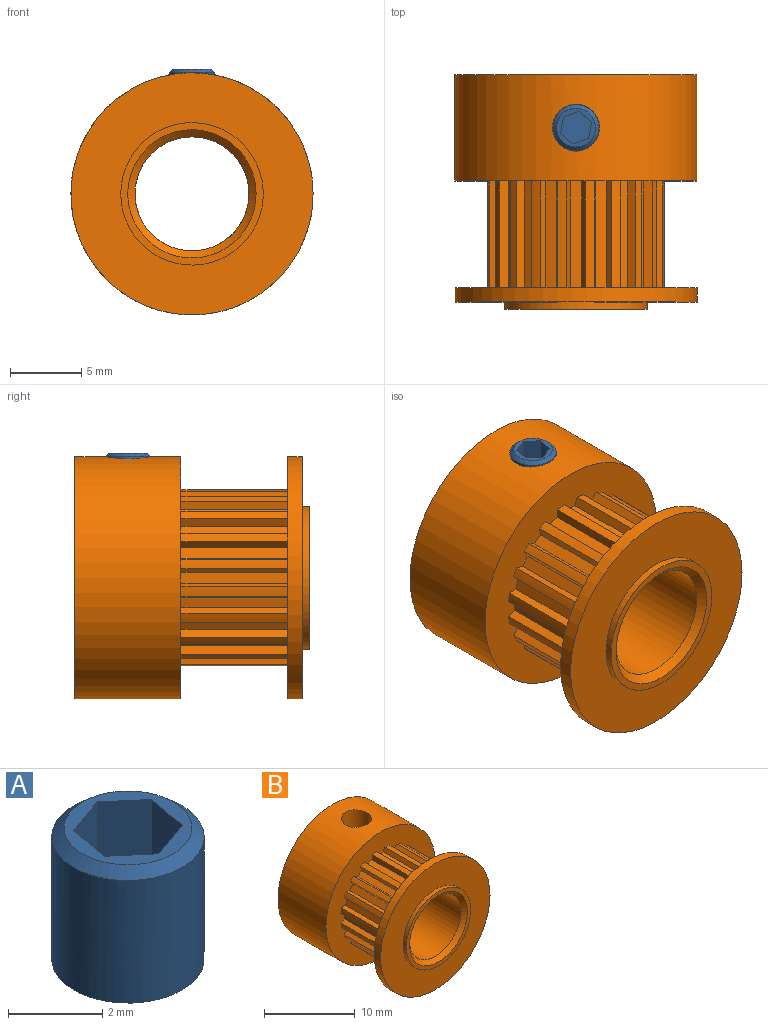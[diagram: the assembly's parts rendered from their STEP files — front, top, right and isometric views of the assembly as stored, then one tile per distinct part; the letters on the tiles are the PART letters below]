
ASSEMBLY  parts=2 mates=1
PART A: 12 faces, bbox 3.2x3.2x4 mm
  f0: plane 3x1.09mm, normal (-0.33,0.94,0), area 3.5mm2, adj f1,f2,f4,f7
  f1: plane 3x0.88mm, normal (0.65,0.76,0), area 3.5mm2, adj f0,f3,f4,f7
  f2: plane 3x1.14mm, normal (-0.98,0.18,0), area 3.5mm2, adj f0,f4,f5,f7
  f3: plane 3x1.14mm, normal (0.98,-0.18,0), area 3.5mm2, adj f1,f4,f6,f7
  f4: plane 2.27x2.18mm, normal (0,0,1), area 3.5mm2, adj f0,f1,f2,f3,f5,f6
  f5: plane 3x0.88mm, normal (-0.65,-0.76,0), area 3.5mm2, adj f2,f4,f6,f7
  f6: plane 3x1.09mm, normal (0.33,-0.94,0), area 3.5mm2, adj f3,f4,f5,f7
  f7: plane 2.71x2.71mm, normal (0,0,1), area 2.3mm2, adj f0,f1,f2,f3,f5,f6,f9
  f8: plane 1.19x1.19mm, normal (0,0,-1), area 1.1mm2, adj f10
  f9: cone r=1.61mm half-angle=48.9deg, axis (0,0,-1), area 3.2mm2, adj f7,f11
  f10: cone r=1.61mm half-angle=59.8deg, axis (0,0,1), area 8.2mm2, adj f8,f11
  f11: cylinder r=1.61mm len=3.23mm, axis (0,0,-1), area 32.3mm2, adj f9,f10
PART B: 92 faces, bbox 17x16.5x17 mm
  f0: plane 7.5x0.63mm, normal (1,0,-0.08), area 4.7mm2, adj f1,f2,f81,f88
  f1: plane 7.5x0.76mm, normal (0.31,0,-0.95), area 6mm2, adj f0,f3,f81,f88
  f2: cylinder r=6.21mm len=7.5mm, axis (0,1,0), area 5mm2, adj f0,f4,f81,f88
  f3: plane 7.5x0.48mm, normal (-0.76,0,-0.65), area 4.7mm2, adj f1,f5,f81,f88
  f4: plane 7.5x0.58mm, normal (-0.92,0,-0.38), area 4.7mm2, adj f2,f6,f81,f88
  f5: cylinder r=6.21mm len=7.5mm, axis (0,1,0), area 5mm2, adj f3,f7,f81,f88
  f6: plane 7.5x0.8mm, normal (0,0,-1), area 6mm2, adj f4,f8,f81,f88
  f7: plane 7.5x0.61mm, normal (0.97,0,0.23), area 4.7mm2, adj f5,f9,f81,f88
  f8: plane 7.5x0.58mm, normal (0.92,0,-0.38), area 4.7mm2, adj f6,f10,f81,f88
  f9: plane 7.5x0.65mm, normal (0.59,0,-0.81), area 6mm2, adj f7,f11,f81,f88
  f10: cylinder r=6.21mm len=7.5mm, axis (0,1,0), area 5mm2, adj f8,f12,f81,f88
  f11: plane 7.5x0.54mm, normal (-0.52,0,-0.85), area 4.7mm2, adj f9,f13,f81,f88
  f12: plane 7.5x0.63mm, normal (-1,0,-0.08), area 4.7mm2, adj f10,f14,f81,f88
  f13: cylinder r=6.21mm len=7.5mm, axis (0,1,0), area 5mm2, adj f11,f15,f81,f88
  f14: plane 7.5x0.76mm, normal (-0.31,0,-0.95), area 6mm2, adj f12,f16,f81,f88
  f15: plane 7.5x0.54mm, normal (0.85,0,0.52), area 4.7mm2, adj f13,f17,f81,f88
  f16: plane 7.5x0.48mm, normal (0.76,0,-0.65), area 4.7mm2, adj f14,f18,f81,f88
  f17: plane 7.5x0.65mm, normal (0.81,0,-0.59), area 6mm2, adj f15,f19,f81,f88
  f18: cylinder r=6.21mm len=7.5mm, axis (0,1,0), area 5mm2, adj f16,f20,f81,f88
  f19: plane 7.5x0.61mm, normal (-0.23,0,-0.97), area 4.7mm2, adj f17,f21,f81,f88
  f20: plane 7.5x0.61mm, normal (-0.97,0,0.23), area 4.7mm2, adj f18,f22,f81,f88
  f21: cylinder r=6.21mm len=7.5mm, axis (0,1,0), area 5mm2, adj f19,f23,f81,f88
  f22: plane 7.5x0.65mm, normal (-0.59,0,-0.81), area 6mm2, adj f20,f24,f81,f88
  f23: plane 7.5x0.48mm, normal (0.65,0,0.76), area 4.7mm2, adj f21,f25,f81,f88
  f24: plane 7.5x0.54mm, normal (0.52,0,-0.85), area 4.7mm2, adj f22,f26,f81,f88
  f25: plane 7.5x0.76mm, normal (0.95,0,-0.31), area 6mm2, adj f23,f27,f81,f88
  f26: cylinder r=6.21mm len=7.5mm, axis (0,1,0), area 5mm2, adj f24,f28,f81,f88
  f27: plane 7.5x0.63mm, normal (0.08,0,-1), area 4.7mm2, adj f25,f29,f81,f88
  f28: plane 7.5x0.54mm, normal (-0.85,0,0.52), area 4.7mm2, adj f26,f30,f81,f88
  f29: cylinder r=6.21mm len=7.5mm, axis (0,1,0), area 5mm2, adj f27,f31,f81,f88
  f30: plane 7.5x0.65mm, normal (-0.81,0,-0.59), area 6mm2, adj f28,f32,f81,f88
  f31: plane 7.5x0.58mm, normal (0.38,0,0.92), area 4.7mm2, adj f29,f33,f81,f88
  f32: plane 7.5x0.61mm, normal (0.23,0,-0.97), area 4.7mm2, adj f30,f34,f81,f88
  f33: plane 7.5x0.8mm, normal (1,0,0), area 6mm2, adj f31,f35,f81,f88
  f34: cylinder r=6.21mm len=7.5mm, axis (0,1,0), area 5mm2, adj f32,f36,f81,f88
  f35: plane 7.5x0.58mm, normal (0.38,0,-0.92), area 4.7mm2, adj f33,f37,f81,f88
  f36: plane 7.5x0.48mm, normal (-0.65,0,0.76), area 4.7mm2, adj f34,f38,f81,f88
  f37: cylinder r=6.21mm len=7.5mm, axis (0,1,0), area 5mm2, adj f35,f39,f81,f88
  f38: plane 7.5x0.76mm, normal (-0.95,0,-0.31), area 6mm2, adj f36,f40,f81,f88
  f39: plane 7.5x0.63mm, normal (0.08,0,1), area 4.7mm2, adj f37,f41,f81,f88
  f40: plane 7.5x0.63mm, normal (-0.08,0,-1), area 4.7mm2, adj f38,f42,f81,f88
  f41: plane 7.5x0.76mm, normal (0.95,0,0.31), area 6mm2, adj f39,f43,f81,f88
  f42: cylinder r=6.21mm len=7.5mm, axis (0,1,0), area 5mm2, adj f40,f44,f81,f88
  f43: plane 7.5x0.48mm, normal (0.65,0,-0.76), area 4.7mm2, adj f41,f45,f81,f88
  f44: plane 7.5x0.58mm, normal (-0.38,0,0.92), area 4.7mm2, adj f42,f46,f81,f88
  f45: cylinder r=6.21mm len=7.5mm, axis (0,1,0), area 5mm2, adj f43,f47,f81,f88
  f46: plane 7.5x0.8mm, normal (-1,0,0), area 6mm2, adj f44,f48,f81,f88
  f47: plane 7.5x0.61mm, normal (-0.23,0,0.97), area 4.7mm2, adj f45,f49,f81,f88
  f48: plane 7.5x0.58mm, normal (-0.38,0,-0.92), area 4.7mm2, adj f46,f50,f81,f88
  f49: plane 7.5x0.65mm, normal (0.81,0,0.59), area 6mm2, adj f47,f51,f81,f88
  f50: cylinder r=6.21mm len=7.5mm, axis (0,1,0), area 5mm2, adj f48,f52,f81,f88
  f51: plane 7.5x0.54mm, normal (0.85,0,-0.52), area 4.7mm2, adj f49,f53,f81,f88
  f52: plane 7.5x0.63mm, normal (-0.08,0,1), area 4.7mm2, adj f50,f54,f81,f88
  f53: cylinder r=6.21mm len=7.5mm, axis (0,1,0), area 5mm2, adj f51,f55,f81,f88
  f54: plane 7.5x0.76mm, normal (-0.95,0,0.31), area 6mm2, adj f52,f56,f81,f88
  f55: plane 7.5x0.54mm, normal (-0.52,0,0.85), area 4.7mm2, adj f53,f57,f81,f88
  f56: plane 7.5x0.48mm, normal (-0.65,0,-0.76), area 4.7mm2, adj f54,f58,f81,f88
  f57: plane 7.5x0.65mm, normal (0.59,0,0.81), area 6mm2, adj f55,f59,f81,f88
  f58: cylinder r=6.21mm len=7.5mm, axis (0,1,0), area 5mm2, adj f56,f60,f81,f88
  f59: plane 7.5x0.61mm, normal (0.97,0,-0.23), area 4.7mm2, adj f57,f61,f81,f88
  f60: plane 7.5x0.61mm, normal (0.23,0,0.97), area 4.7mm2, adj f58,f62,f81,f88
  f61: cylinder r=6.21mm len=7.5mm, axis (0,1,0), area 5mm2, adj f59,f63,f81,f88
  f62: plane 7.5x0.65mm, normal (-0.81,0,0.59), area 6mm2, adj f60,f64,f81,f88
  f63: plane 7.5x0.48mm, normal (-0.76,0,0.65), area 4.7mm2, adj f61,f65,f81,f88
  f64: plane 7.5x0.54mm, normal (-0.85,0,-0.52), area 4.7mm2, adj f62,f66,f81,f88
  f65: plane 7.5x0.76mm, normal (0.31,0,0.95), area 6mm2, adj f63,f67,f81,f88
  f66: cylinder r=6.21mm len=7.5mm, axis (0,1,0), area 5mm2, adj f64,f68,f81,f88
  f67: plane 7.5x0.63mm, normal (1,0,0.08), area 4.7mm2, adj f65,f69,f81,f88
  f68: plane 7.5x0.54mm, normal (0.52,0,0.85), area 4.7mm2, adj f66,f70,f81,f88
  f69: cylinder r=6.21mm len=7.5mm, axis (0,1,0), area 5mm2, adj f67,f71,f81,f88
  f70: plane 7.5x0.65mm, normal (-0.59,0,0.81), area 6mm2, adj f68,f72,f81,f88
  f71: plane 7.5x0.58mm, normal (-0.92,0,0.38), area 4.7mm2, adj f69,f74,f81,f88
  f72: plane 7.5x0.61mm, normal (-0.97,0,-0.23), area 4.7mm2, adj f70,f75,f81,f88
  f73: plane 17x17mm, normal (0,-1,0), area 148.4mm2, adj f76,f77
  f74: plane 7.5x0.8mm, normal (0,0,1), area 6mm2, adj f71,f78,f81,f88
  f75: cylinder r=6.21mm len=7.5mm, axis (0,1,0), area 5mm2, adj f72,f79,f81,f88
  f76: cylinder r=5mm len=10mm, axis (0,1,0), area 15.7mm2, adj f73,f80
  f77: cylinder r=8.5mm len=17mm, axis (0,-1,0), area 53.4mm2, adj f73,f81
  f78: plane 7.5x0.58mm, normal (0.92,0,0.38), area 4.7mm2, adj f74,f81,f82,f88
  f79: plane 7.5x0.48mm, normal (0.76,0,0.65), area 4.7mm2, adj f75,f81,f83,f88
  f80: plane 10x10mm, normal (0,-1,0), area 14.9mm2, adj f76,f84
  f81: plane 17x17mm, normal (0,1,0), area 118.3mm2, adj f0,f1,f2,f3,f4,f5,f6,f7
  f82: cylinder r=6.21mm len=7.5mm, axis (0,1,0), area 5mm2, adj f78,f81,f85,f88
  f83: plane 7.5x0.76mm, normal (-0.31,0,0.95), area 6mm2, adj f79,f81,f85,f88
  f84: cone r=4.5mm half-angle=45deg, axis (0,-1,0), area 18.9mm2, adj f80,f87
  f85: plane 7.5x0.63mm, normal (-1,0,0.08), area 4.7mm2, adj f81,f82,f83,f88
  f86: cone r=4.5mm half-angle=45deg, axis (0,1,0), area 18.9mm2, adj f87,f89
  f87: cylinder r=4mm len=15.45mm, axis (0,-1,0), area 379.6mm2, adj f84,f86,f90
  f88: plane 17x17mm, normal (0,-1,0), area 118.3mm2, adj f0,f1,f2,f3,f4,f5,f6,f7
  f89: plane 17x17mm, normal (0,1,0), area 163.4mm2, adj f86,f91
  f90: cylinder r=1.65mm len=4.86mm, axis (0,0,-1), area 47.6mm2, adj f87,f91
  f91: cylinder r=8.5mm len=17mm, axis (0,1,0), area 389.3mm2, adj f88,f89,f90
PLACE A t=(1.65,0,1.16)mm
PLACE B t=(1.65,0,1.4)mm
MATE fastened B.f90 <-> A.f9  axis (0,0,-1) through (1.65,-3.72,9.93)mm
